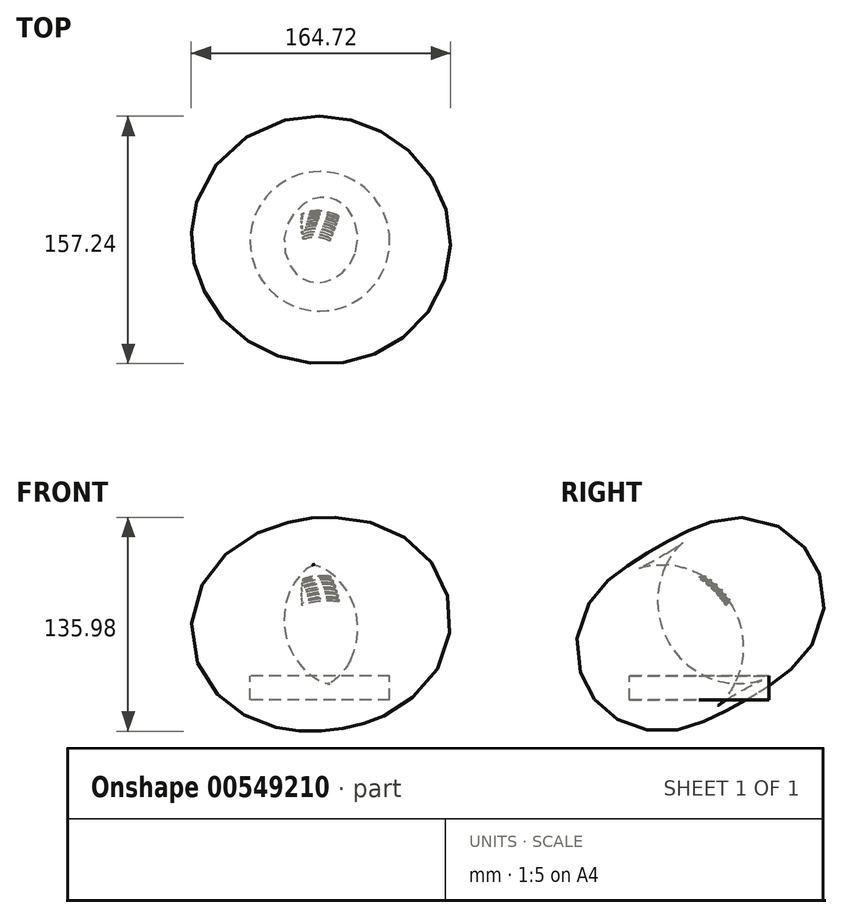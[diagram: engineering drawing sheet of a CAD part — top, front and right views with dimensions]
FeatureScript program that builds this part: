
annotation { "Feature Type Name" : "Feature", "Feature Type Description" : "" }
export const myFeature = defineFeature(function(context is Context, id is Id, definition is map)
    precondition{}
    {
        {
            var Q0;
            Q0=qCreatedBy(makeId("Front.planeOp"),FACE);
            var sketch = newSketch(context, id + "F0", { "sketchPlane" : qUnion([Q0])});
            skLineSegment(sketch, "E0", {"start": v(-43.8, 0) * mm, "end": v(43.8, 0) * mm});
            skArc(sketch, "E1", {"start": v(43.8, 0) * mm, "mid": v(0, 23.24) * mm, "end": v(-43.8, 0) * mm});
            skSolve(sketch);
        }
        {
            var Q0;
            Q0=makeQuery(id+"F0.imprint","IMPRINT",FACE,{"disambiguationData":[TD([[makeQuery(id+"F0.imprint","IMPRINT",EDGE,{"derivedFrom":sQuery(id+"F0.wireOp",EDGE,"E0")}),1.0]])]});
            var Q1;
            Q1=sQuery(id+"F0.wireOp",EDGE,"E0");
            revolve(context, id + "F1", {"entities" : qUnion([Q0]), "axis" : qUnion([Q1]), "revolveType" : RevolveType.FULL});
        }
        {
            var Q0;
            Q0=qCreatedBy(makeId("Front.planeOp"),FACE);
            var sketch = newSketch(context, id + "F2", { "sketchPlane" : qUnion([Q0])});
            skArc(sketch, "E2.0", {"start": v(43.8, 0) * mm, "mid": v(0, 23.24) * mm, "end": v(-43.8, 0) * mm});
            skLineSegment(sketch, "E3", {"start": v(-25.6, 16.62) * mm, "end": v(-25.13, 18.12) * mm});
            skLineSegment(sketch, "E4", {"start": v(-25.13, 18.12) * mm, "end": v(-23.65, 17.65) * mm});
            skLineSegment(sketch, "E5", {"start": v(-23.65, 17.65) * mm, "end": v(-21.86, 18.5) * mm});
            skLineSegment(sketch, "E6", {"start": v(-21.86, 18.5) * mm, "end": v(-21.12, 20.01) * mm});
            skLineSegment(sketch, "E7", {"start": v(-21.12, 20.01) * mm, "end": v(-19.33, 19.58) * mm});
            skLineSegment(sketch, "E8", {"start": v(-19.33, 19.58) * mm, "end": v(-17.47, 20.27) * mm});
            skLineSegment(sketch, "E9", {"start": v(-17.47, 20.27) * mm, "end": v(-17, 21.56) * mm});
            skLineSegment(sketch, "E10", {"start": v(-17, 21.56) * mm, "end": v(-14.88, 21.1) * mm});
            skLineSegment(sketch, "E11", {"start": v(-14.88, 21.1) * mm, "end": v(-12.92, 21.63) * mm});
            skLineSegment(sketch, "E12", {"start": v(-12.92, 21.63) * mm, "end": v(-12.37, 22.87) * mm});
            skLineSegment(sketch, "E13", {"start": v(-12.37, 22.87) * mm, "end": v(-10.72, 22.14) * mm});
            skLineSegment(sketch, "E14", {"start": v(-10.72, 22.14) * mm, "end": v(-9.29, 22.42) * mm});
            skLineSegment(sketch, "E15", {"start": v(-9.29, 22.42) * mm, "end": v(-8.53, 23.39) * mm});
            skLineSegment(sketch, "E16", {"start": v(-8.53, 23.39) * mm, "end": v(-6.8, 22.8) * mm});
            skLineSegment(sketch, "E17", {"start": v(-6.8, 22.8) * mm, "end": v(-5.66, 22.93) * mm});
            skLineSegment(sketch, "E18", {"start": v(-5.66, 22.93) * mm, "end": v(-4.64, 24.08) * mm});
            skLineSegment(sketch, "E19", {"start": v(-4.64, 24.08) * mm, "end": v(-3.57, 23.12) * mm});
            skSolve(sketch);
        }
        {
            var Q0;
            {var subQ0=sQuery(id+"F2.wireOp",EDGE,"E3");Q0=makeQuery(id+"F2.imprint","IMPRINT",FACE,{"disambiguationData":[TD([[makeQuery(id+"F2.imprint","IMPRINT",EDGE,{"derivedFrom":subQ0}),-1.0]])]});}
            var Q1;
            {var subQ0=sQuery(id+"F2.wireOp",EDGE,"E6");Q1=makeQuery(id+"F2.imprint","IMPRINT",FACE,{"disambiguationData":[TD([[makeQuery(id+"F2.imprint","IMPRINT",EDGE,{"derivedFrom":subQ0}),-1.0]])]});}
            var Q2;
            {var subQ0=sQuery(id+"F2.wireOp",EDGE,"E9");Q2=makeQuery(id+"F2.imprint","IMPRINT",FACE,{"disambiguationData":[TD([[makeQuery(id+"F2.imprint","IMPRINT",EDGE,{"derivedFrom":subQ0}),-1.0]])]});}
            var Q3;
            {var subQ0=sQuery(id+"F2.wireOp",EDGE,"E12");Q3=makeQuery(id+"F2.imprint","IMPRINT",FACE,{"disambiguationData":[TD([[makeQuery(id+"F2.imprint","IMPRINT",EDGE,{"derivedFrom":subQ0}),-1.0]])]});}
            var Q4;
            {var subQ0=sQuery(id+"F2.wireOp",EDGE,"E15");Q4=makeQuery(id+"F2.imprint","IMPRINT",FACE,{"disambiguationData":[TD([[makeQuery(id+"F2.imprint","IMPRINT",EDGE,{"derivedFrom":subQ0}),-1.0]])]});}
            var Q5;
            {var subQ0=sQuery(id+"F2.wireOp",EDGE,"E18");Q5=makeQuery(id+"F2.imprint","IMPRINT",FACE,{"disambiguationData":[TD([[makeQuery(id+"F2.imprint","IMPRINT",EDGE,{"derivedFrom":subQ0}),-1.0]])]});}
            var Q6;
            Q6=sQuery(id+"F0.wireOp",EDGE,"E0");
            revolve(context, id + "F3", {"operationType" : NewBodyOperationType.ADD, "entities" : qUnion([Q0, Q1, Q2, Q3, Q4, Q5]), "axis" : qUnion([Q6]), "revolveType" : RevolveType.TWO_DIRECTIONS, "angle" : 30 * degree, "angleBack" : 330 * degree});
        }
        {
            var Q0;
            Q0=makeQuery(id+"F1.opRevolve","SWEPT_BODY",BODY,{"disambiguationData":[OSD([sQuery(id+"F0.wireOp",EDGE,"E0"),sQuery(id+"F0.wireOp",EDGE,"E1")])]});
            var Q1;
            Q1=makeQuery(id+"F3.opRevolve","CAP_EDGE",EDGE,{"disambiguationData":[OSD([sQuery(id+"F2.wireOp",EDGE,"E19")])],"isStart":false});
            transform(context, id + "F4", {"entities" : qUnion([Q0]), "transformType" : TransformType.ROTATION, "transformAxis" : qUnion([Q1]), "angle" : 180 * degree, "makeCopy" : false});
        }
        {
            var Q0;
            Q0=makeQuery(id+"F1.opRevolve","SWEPT_BODY",BODY,{"disambiguationData":[OSD([sQuery(id+"F0.wireOp",EDGE,"E0"),sQuery(id+"F0.wireOp",EDGE,"E1")])]});
            var Q1;
            Q1=makeQuery(id+"F1.opRevolve","SWEPT_FACE",FACE,{"disambiguationData":[OSD([sQuery(id+"F0.wireOp",EDGE,"E1")])]});
            transform(context, id + "F5", {"entities" : qUnion([Q0]), "transformType" : TransformType.ROTATION, "transformAxis" : qUnion([Q1]), "angle" : 90 * degree, "oppositeDirection" : true, "makeCopy" : false});
        }
        {
            var Q0;
            Q0=makeQuery(id+"F1.opRevolve","SWEPT_BODY",BODY,{"disambiguationData":[OSD([sQuery(id+"F0.wireOp",EDGE,"E0"),sQuery(id+"F0.wireOp",EDGE,"E1")])]});
            var Q1;
            Q1=makeQuery(id+"F1.opRevolve","SWEPT_FACE",FACE,{"disambiguationData":[OSD([sQuery(id+"F0.wireOp",EDGE,"E1")])]});
            transform(context, id + "F6", {"entities" : qUnion([Q0]), "transformType" : TransformType.ROTATION, "transformAxis" : qUnion([Q1]), "angle" : 330 * degree, "makeCopy" : false});
        }
        {
            var Q0;
            Q0=qCreatedBy(makeId("Top.planeOp"),FACE);
            var sketch = newSketch(context, id + "F7", { "sketchPlane" : qUnion([Q0])});
            skCircle(sketch, "E20", {"center": v(-49.18, -9.42) * mm, "radius": 44.3 * mm});
            skSolve(sketch);
        }
        {
            var Q0;
            Q0 = qSketchRegion(id + "F7", true);
            extrude(context, id + "F8", {"entities" : qUnion([Q0]), "oppositeDirection" : true, "depth" : 15.24 * mm, "offsetDistance" : 25.4 * mm});
        }
        {
            var Q0;
            Q0=makeQuery(id+"F8.opExtrude","SWEPT_BODY",BODY,{"disambiguationData":[OSD([sQuery(id+"F7.wireOp",EDGE,"E20")])]});
            transform(context, id + "F9", {"entities" : qUnion([Q0]), "transformType" : TransformType.TRANSLATION_3D, "dx" : 68.33 * mm, "dy" : -2.54 * mm, "dz" : -13.72 * mm, "makeCopy" : false});
        }
    });
